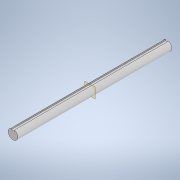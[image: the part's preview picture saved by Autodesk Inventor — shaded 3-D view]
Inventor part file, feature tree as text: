
AUTODESK INVENTOR PART (.ipt)
format: ipt  version: 2021.1 (Build 251245000, 245)  size: 101,888 bytes
history: native  units: in
note: dims shown in document units (in); Inventor stores cm internally (conversion verified against a paired STEP export)
features: extrude x1, sketch x1
ambient origin geometry x8: Origin, YZ Plane, XZ Plane, XY Plane, X Axis, Y Axis, Z Axis, Center Point
bodies: Solid1 (feature_tree)
feature tree (2):
  extrude  "Extrusion1"  Depth=6.0in
  sketch  "Sketch1"  dims[d0=0.375in d1=0.0469in d2=0.0628in d3=6.0in d4=0.0in]
